# Revit family: Haworth_XSeries_StorageCabinet_21h
name_source: partatom
category: Furniture Systems
revit_build: Autodesk Revit 2018 (Build: 20170223_1515(x64)
units: mm (PartAtom-declared; Revit-internal decimal feet)

## family parameters
Always vertical = Yes
Cut with Voids When Loaded = No
OmniClass Number = 23.40.70.14.64.21
OmniClass Title = Systems Furniture
Part Type = Normal
Room Calculation Point = No
Round Connector Dimension = Use Diameter
Shared = No
Work Plane-Based = No

## types (1)
- 18d 36w 21h
    # of Shelves = 1
    Actaul # of Shelves = 2
    Actual Depth = 18 3/4"
    Actual Height = 21 1/2"
    Actual Width = 35 7/8"
    Assembly Code = E2020200
    Bar Pull = No
    Cabinet Height = 21 1/2"
    Classic Pull = No
    Crescent Pull = No
    Custom Size = No
    Description = Haworth XSeries Storage Cabinet - 18d 36w 27h
    Door Height = 18 3/8"
    Door Width = 17 3/16"
    Doors = Yes
    J Pull = No
    Linear Pull = Yes
    Manufacturer = Haworth
    Max # of Shelves = 4
    Max. Height = 63 1/2"
    Max. Width = 47 7/8"
    Min. Height = 27 1/2"
    Min. Width = 29 7/8"
    Model = JSPY-0236
    Pull Ellipse = No
    Pull Finish = Haworth _ Metal _ Brushed Aluminum
    Pull Height = 9 3/16"
    Radius Pull = No
    Revision Number = 6
    Shelf Depth = 17 1/4"
    Shelf Spacing = 6 1/8"
    Shelf Width = 34 3/8"
    Shelves = No
    Single Shelf = Yes
    Size = Verify Final Dim. w/ Haworth
    Standard Widths = 30, 36, 42 in.
    Sustainability Info = https://www.haworth.com
    Taper Pull = No
    URL = http://www.haworth.com
    URL - Product = https://www.haworth.com
    Warranty = http://www.haworth.com
    Width = 36"

## geometry (parser evidence)
native form markers: Sweep x11
no freeform markers — native parametric forms only
